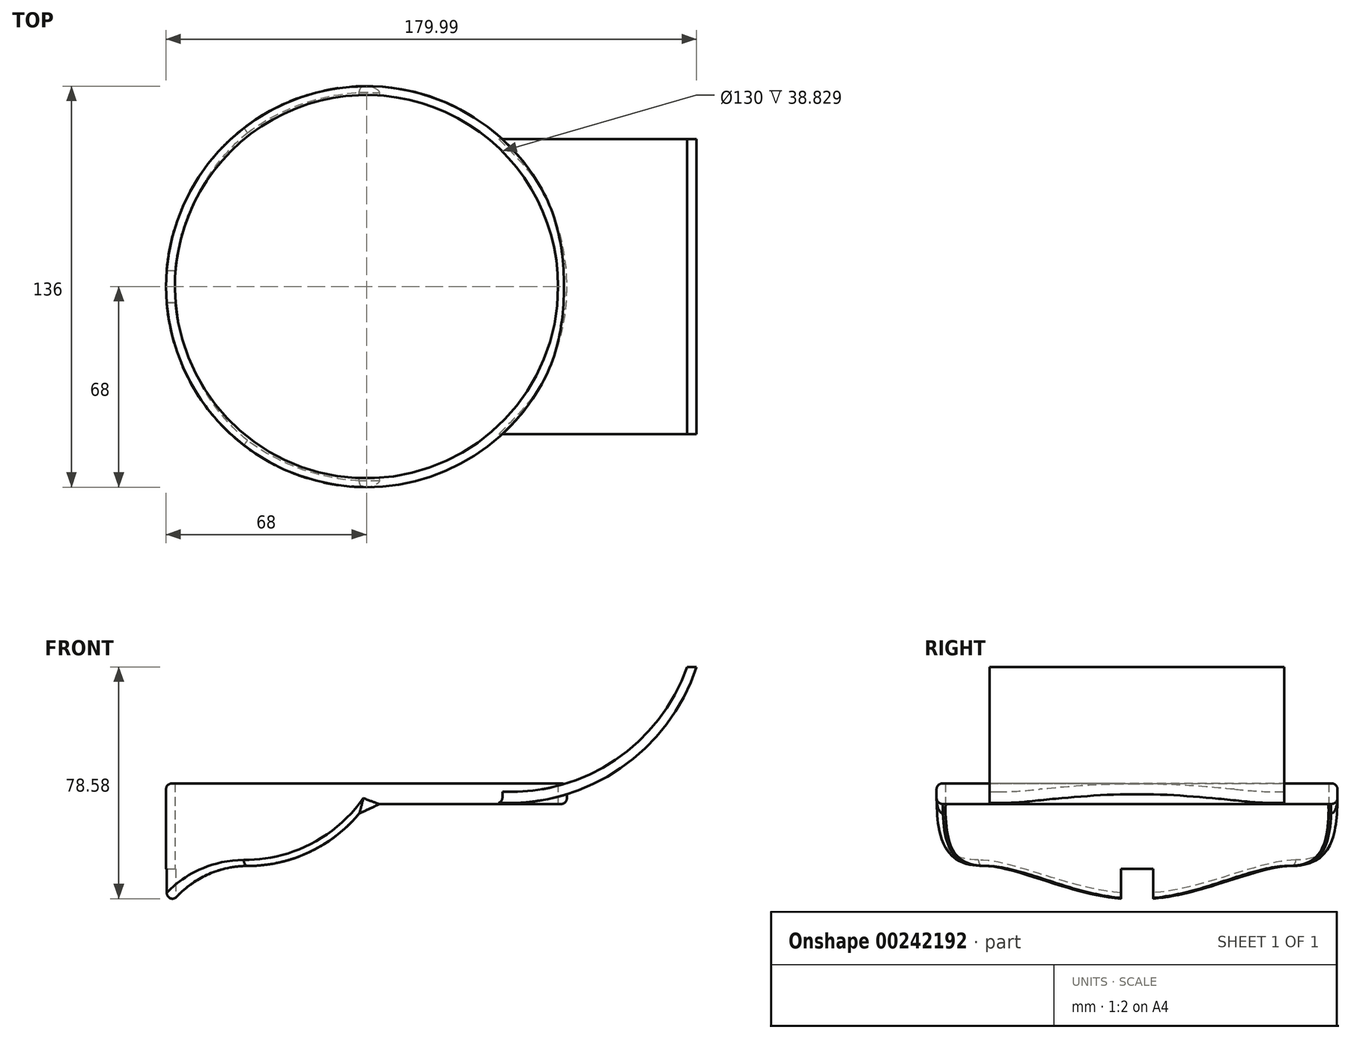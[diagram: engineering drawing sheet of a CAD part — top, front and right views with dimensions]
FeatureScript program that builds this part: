
annotation { "Feature Type Name" : "Feature", "Feature Type Description" : "" }
export const myFeature = defineFeature(function(context is Context, id is Id, definition is map)
    precondition{}
    {
        {
            var Q0;
            Q0=qCreatedBy(makeId("Top.planeOp"),FACE);
            var sketch = newSketch(context, id + "F0", { "sketchPlane" : qUnion([Q0])});
            skCircle(sketch, "E0", {"center": v(0, 0) * mm, "radius": 65 * mm});
            skCircle(sketch, "E1", {"center": v(0, 0) * mm, "radius": 68 * mm});
            skSolve(sketch);
        }
        {
            var Q0;
            Q0 = qSketchRegion(id + "F0", true);
            extrude(context, id + "F1", {"entities" : qUnion([Q0]), "depth" : 40 * mm});
        }
        {
            var Q0;
            Q0=qCreatedBy(makeId("Right.planeOp"),FACE);
            var sketch = newSketch(context, id + "F2", { "sketchPlane" : qUnion([Q0])});
            skLineSegment(sketch, "E2.bottom", {"start": v(-5.5, 0) * mm, "end": v(5.5, 0) * mm});
            skLineSegment(sketch, "E2.top", {"start": v(-5.5, 11) * mm, "end": v(5.5, 11) * mm});
            skLineSegment(sketch, "E2.left", {"start": v(-5.5, 0) * mm, "end": v(-5.5, 11) * mm});
            skLineSegment(sketch, "E2.right", {"start": v(5.5, 0) * mm, "end": v(5.5, 11) * mm});
            skSolve(sketch);
        }
        {
            var Q0;
            Q0=makeQuery(id+"F2.imprint","IMPRINT",FACE,{"disambiguationData":[TD([[makeQuery(id+"F2.imprint","IMPRINT",EDGE,{"derivedFrom":sQuery(id+"F2.wireOp",EDGE,"E2.bottom")}),1.0]])]});
            extrude(context, id + "F3", {"entities" : qUnion([Q0]), "operationType" : NewBodyOperationType.REMOVE, "oppositeDirection" : true, "depth" : 90 * mm});
        }
        {
            var Q0;
            Q0=qCreatedBy(makeId("Front.planeOp"),FACE);
            var sketch = newSketch(context, id + "F4", { "sketchPlane" : qUnion([Q0])});
            skLineSegment(sketch, "E3", {"start": v(68.4, 0) * mm, "end": v(68.4, 12) * mm});
            skLineSegment(sketch, "E4", {"start": v(-65.64, 0) * mm, "end": v(68.4, 0) * mm});
            skArc(sketch, "E5", {"start": v(-40.39, 12) * mm, "mid": v(-54.37, 8.85) * mm, "end": v(-65.64, 0) * mm});
            skLineSegment(sketch, "E6", {"start": v(68.4, 12) * mm, "end": v(68.4, 33) * mm});
            skLineSegment(sketch, "E7", {"start": v(68.4, 33) * mm, "end": v(0, 33) * mm});
            skArc(sketch, "E8", {"start": v(-40.39, 12) * mm, "mid": v(-17.63, 17.56) * mm, "end": v(0, 33) * mm});
            skArc(sketch, "E9", {"start": v(44.61, 37.28) * mm, "mid": v(83.8, 47.56) * mm, "end": v(108.72, 79.48) * mm});
            skArc(sketch, "E10", {"start": v(44.13, 33.44) * mm, "mid": v(85.88, 44.93) * mm, "end": v(111.99, 79.48) * mm});
            skLineSegment(sketch, "E11", {"start": v(44.61, 37.28) * mm, "end": v(44.13, 33.44) * mm});
            skLineSegment(sketch, "E12", {"start": v(111.99, 79.48) * mm, "end": v(108.72, 79.48) * mm});
            skSolve(sketch);
        }
        {
            var Q0;
            Q0=makeQuery(id+"F4.imprint","IMPRINT",FACE,{"disambiguationData":[TD([[makeQuery(id+"F4.imprint","IMPRINT",EDGE,{"derivedFrom":sQuery(id+"F4.wireOp",EDGE,"E3")}),1.0]])]});
            extrude(context, id + "F5", {"entities" : qUnion([Q0]), "operationType" : NewBodyOperationType.REMOVE, "endBound" : BoundingType.SYMMETRIC, "depth" : 200 * mm});
        }
        {
            var Q0;
            Q0=makeQuery(id+"F5.boolean.opBoolean","INTERSECT",EDGE,{"derivedFrom":[makeQuery(id+"F1.opExtrude","SWEPT_FACE",FACE,{"disambiguationData":[OSD([sQuery(id+"F0.wireOp",EDGE,"E1")])]}),makeQuery(id+"F5.opExtrude","SWEPT_FACE",FACE,{"disambiguationData":[OSD([sQuery(id+"F4.wireOp",EDGE,"E7")])]})]});
            var Q1;
            Q1=makeQuery(id+"F1.opExtrude","CAP_EDGE",EDGE,{"disambiguationData":[OSD([sQuery(id+"F0.wireOp",EDGE,"E1")])],"isStart":false});
            var Q2;
            Q2=makeQuery(id+"F5.boolean.opBoolean","INTERSECT",EDGE,{"disambiguationData":[OD(1.0)],"derivedFrom":[makeQuery(id+"F1.opExtrude","SWEPT_FACE",FACE,{"disambiguationData":[OSD([sQuery(id+"F0.wireOp",EDGE,"E1")])]}),makeQuery(id+"F5.opExtrude","SWEPT_FACE",FACE,{"disambiguationData":[OSD([sQuery(id+"F4.wireOp",EDGE,"E8")])]})]});
            var Q3;
            Q3=makeQuery(id+"F5.boolean.opBoolean","INTERSECT",EDGE,{"disambiguationData":[OD(0.0)],"derivedFrom":[makeQuery(id+"F1.opExtrude","SWEPT_FACE",FACE,{"disambiguationData":[OSD([sQuery(id+"F0.wireOp",EDGE,"E1")])]}),makeQuery(id+"F5.opExtrude","SWEPT_FACE",FACE,{"disambiguationData":[OSD([sQuery(id+"F4.wireOp",EDGE,"E8")])]})]});
            fillet(context, id + "F6", {"entities" : qUnion([Q0, Q1, Q2, Q3]), "radius" : 2 * mm, "tangentPropagation" : true, "allowEdgeOverflow" : false});
        }
        {
            var Q0;
            {var subQ0=makeQuery(id+"F1.opExtrude","SWEPT_FACE",FACE,{"disambiguationData":[OSD([sQuery(id+"F0.wireOp",EDGE,"E1")])]});Q0=makeQuery(id+"F6.opFillet","BLEND_EDGE",EDGE,{"blendedFrom":[makeQuery(id+"F5.boolean.opBoolean","INTERSECT",EDGE,{"derivedFrom":[subQ0,makeQuery(id+"F5.opExtrude","SWEPT_FACE",FACE,{"disambiguationData":[OSD([sQuery(id+"F4.wireOp",EDGE,"E7")])]})]}),makeQuery(id+"F5.boolean.opBoolean","INTERSECT",EDGE,{"disambiguationData":[OD(0.0)],"derivedFrom":[subQ0,makeQuery(id+"F5.opExtrude","SWEPT_FACE",FACE,{"disambiguationData":[OSD([sQuery(id+"F4.wireOp",EDGE,"E8")])]})]})],"blendedInto":[]});}
            var Q1;
            Q1=makeQuery(id+"F5.boolean.opBoolean","COPY",EDGE,{"disambiguationData":[OD(1.0)],"derivedFrom":makeQuery(id+"F5.opExtrude","SWEPT_EDGE",EDGE,{"disambiguationData":[OSD([sQuery(id+"F4.wireOp",EDGE,"E7"),sQuery(id+"F4.wireOp",EDGE,"E8")])]})});
            var Q2;
            Q2=makeQuery(id+"F5.boolean.opBoolean","COPY",EDGE,{"disambiguationData":[OD(0.0)],"derivedFrom":makeQuery(id+"F5.opExtrude","SWEPT_EDGE",EDGE,{"disambiguationData":[OSD([sQuery(id+"F4.wireOp",EDGE,"E7"),sQuery(id+"F4.wireOp",EDGE,"E8")])]})});
            var Q3;
            {var subQ0=makeQuery(id+"F1.opExtrude","SWEPT_FACE",FACE,{"disambiguationData":[OSD([sQuery(id+"F0.wireOp",EDGE,"E1")])]});Q3=makeQuery(id+"F6.opFillet","BLEND_EDGE",EDGE,{"blendedFrom":[makeQuery(id+"F5.boolean.opBoolean","INTERSECT",EDGE,{"derivedFrom":[subQ0,makeQuery(id+"F5.opExtrude","SWEPT_FACE",FACE,{"disambiguationData":[OSD([sQuery(id+"F4.wireOp",EDGE,"E7")])]})]}),makeQuery(id+"F5.boolean.opBoolean","INTERSECT",EDGE,{"disambiguationData":[OD(1.0)],"derivedFrom":[subQ0,makeQuery(id+"F5.opExtrude","SWEPT_FACE",FACE,{"disambiguationData":[OSD([sQuery(id+"F4.wireOp",EDGE,"E8")])]})]})],"blendedInto":[]});}
            chamfer(context, id + "F7", {"entities" : qUnion([Q0, Q1, Q2, Q3]), "width" : 9 * mm, "tangentPropagation" : true});
        }
        {
            var Q0;
            Q0=makeQuery(id+"F4.imprint","IMPRINT",FACE,{"disambiguationData":[TD([[makeQuery(id+"F4.imprint","IMPRINT",EDGE,{"derivedFrom":sQuery(id+"F4.wireOp",EDGE,"E9")}),-1.0]])]});
            extrude(context, id + "F8", {"entities" : qUnion([Q0]), "operationType" : NewBodyOperationType.ADD, "endBound" : BoundingType.SYMMETRIC, "depth" : 100 * mm});
        }
        {
            var Q0;
            Q0=makeQuery(id+"F0.imprint","IMPRINT",FACE,{"disambiguationData":[TD([[makeQuery(id+"F0.imprint","IMPRINT",EDGE,{"derivedFrom":sQuery(id+"F0.wireOp",EDGE,"E0")}),1.0]])]});
            extrude(context, id + "F9", {"entities" : qUnion([Q0]), "operationType" : NewBodyOperationType.REMOVE, "depth" : 43 * mm});
        }
    });
